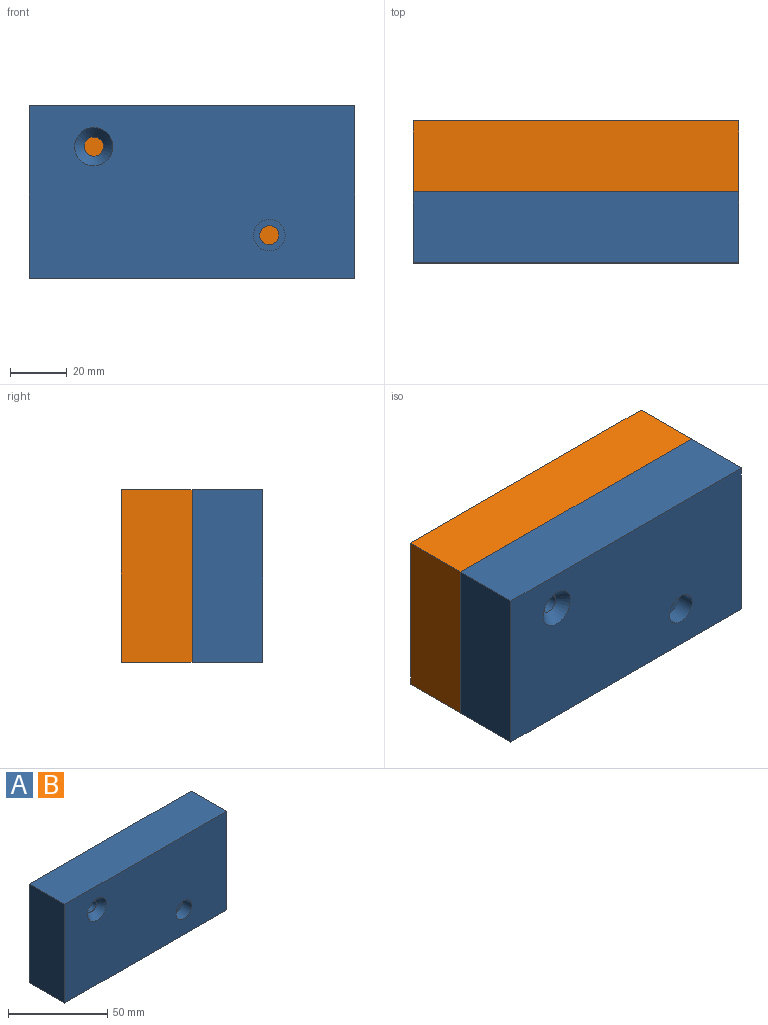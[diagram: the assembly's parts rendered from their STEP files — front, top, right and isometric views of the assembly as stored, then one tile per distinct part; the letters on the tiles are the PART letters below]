
ASSEMBLY  parts=2 mates=1
PART A: 11 faces, bbox 114.8x25x60.8 mm
  f0: plane 60.8x25mm, normal (1,0,0), area 1520.1mm2, adj f1,f3,f4,f5
  f1: plane 114.77x25mm, normal (0,0,1), area 2869.2mm2, adj f0,f2,f4,f5
  f2: plane 60.8x25mm, normal (-1,0,0), area 1520.1mm2, adj f1,f3,f4,f5
  f3: plane 114.77x25mm, normal (0,0,-1), area 2869.2mm2, adj f0,f2,f4,f5
  f4: plane 114.77x60.8mm, normal (0,-1,0), area 6738.3mm2, adj f0,f1,f2,f3,f7,f10
  f5: plane 114.77x60.8mm, normal (0,1,0), area 6906.5mm2, adj f0,f1,f2,f3,f6,f8
  f6: cylinder r=3.38mm len=21.13mm, axis (0,-1,0), area 448.5mm2, adj f5,f7
  f7: cone r=3.38mm half-angle=41deg, axis (0,-1,0), area 163.1mm2, adj f4,f6
  f8: cylinder r=3.38mm len=18.65mm, axis (0,-1,0), area 395.9mm2, adj f5,f9
  f9: plane 11.11x11.11mm, normal (0,-1,0), area 61.1mm2, adj f8,f10
  f10: cylinder r=5.56mm len=11.11mm, axis (0,-1,0), area 221.7mm2, adj f4,f9
PART B: same geometry as A
PLACE A t=(160.42,116.76,17.46)mm
PLACE B rot(axis=(1,0,0),180deg) t=(160.42,116.76,17.45)mm
MATE planar B.f5 <-> A.f5  axis (0,-1,0) through (160.46,116.76,17.45)mm
